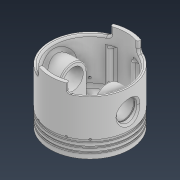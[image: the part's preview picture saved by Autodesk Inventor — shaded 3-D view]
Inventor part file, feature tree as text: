
AUTODESK INVENTOR PART (.ipt)
format: ipt  version: 2022 (Build 260153000, 153)  size: 603,136 bytes
history: native  units: mm
features: sketch x10, extrude x10, plane x8, fillet x5, mirror x3, other x2, projected_geometry x2, hole x1, chamfer x1, pattern_circular x1
ambient origin geometry x8: Origin, YZ Plane, XZ Plane, XY Plane, X Axis, Y Axis, Z Axis, Center Point
bodies: Solid1 (feature_tree)
feature tree (43):
  sketch  "Sketch1"  dims[d0=85.5mm d1=78.0mm]
  extrude  "Extrusion1"  Depth=78.0mm
  extrude  "Extrusion2"  Depth=10.0mm TaperAngle=0.0deg
  plane  "Work Plane1"
  extrude  "Extrusion3"  Depth=10.0mm
  extrude  "Extrusion4"  Depth=2.5mm
  extrude  "Extrusion5"  Depth=40.0mm TaperAngle=0.0deg
  hole  "Hole1"  [1 undecoded]
  other  "Full Round Fillet1"
  other  "Full Round Fillet2"
  fillet  "Fillet1"  Radius=40.0mm
  fillet  "Fillet2"  Radius=15.0mm
  fillet  "Fillet3"  Radius=15.0mm
  fillet  "Fillet4"  Radius=1.0mm
  fillet  "Fillet5"  Radius=3.0mm
  chamfer  "Chamfer1"  Distance=2.0mm Angle=45.0deg
  plane  "Work Plane3"
  plane  "Work Plane4"
  extrude  "Extrusion8"  [1 undecoded]
  plane  "Work Plane5"
  extrude  "Extrusion9"  [1 undecoded]
  plane  "Work Plane6"
  extrude  "Extrusion10"  Depth=1.2mm
  plane  "Work Plane7"
  extrude  "Extrusion11"  Depth=1.2mm TaperAngle=0.0deg
  pattern_circular  "Circular Pattern1"  [2 undecoded]
  mirror  "Mirror2"
  mirror  "Mirror3"
  plane  "Work Plane8"
  extrude  "Extrusion12"  Depth=1.2mm TaperAngle=0.0deg
  mirror  "Mirror4"
  sketch  "Sketch2"  dims[d2=68.0mm d3=0.0mm d4=10.0mm d5=0.0mm]
  sketch  "Sketch3"  dims[d6=10.0mm d7=30.0mm]
  sketch  "Sketch4"  dims[d8=0.0mm d9=0.0mm d10=2.5mm]
  sketch  "Sketch6"  dims[d11=78.0mm d12=40.0mm d13=0.0mm]
  plane  "Work Plane2"
  sketch  "Sketch8"  dims[d14=35.0mm d15=30.0mm d16=40.0mm d17=0.0mm d18=15.0mm d19=15.0mm]
  sketch  "Sketch9"  dims[d20=22.0mm d21=6.0mm d22=4.0mm d23=2.0mm d24=90.0deg d25=8.0mm d26=20.594885mm d27=1.0mm d28=3.0mm]
  sketch  "Sketch10"  dims[d29=3.0mm]
  projected_geometry  "Projected Loop1"
  sketch  "Sketch11"  dims[d30=3.0mm]
  projected_geometry  "Projected Loop2"
  sketch  "Sketch12"  dims[d31=2.0mm d32=2.0mm d33=2.0mm d34=45.0deg d35=-2.0mm d41=-7.0mm d42=83.0mm d43=2.0mm d44=0.0mm d45=-3.0mm d46=2.0mm d47=0.0mm d48=-3.0mm d49=3.0mm d50=0.0mm d51=2.5mm d52=29.25mm d53=6.25mm d54=0.0mm d55=0.0mm d56=20.0mm d57=-4.363323mm d59=36.0mm d60=24.0mm d61=1.2mm d62=0.0mm]
note: 5 required parameter values undecoded (feature->parameter linkage not recoverable at this tier; creation-order binding heuristic only, values carry confidence <= 0.55)
